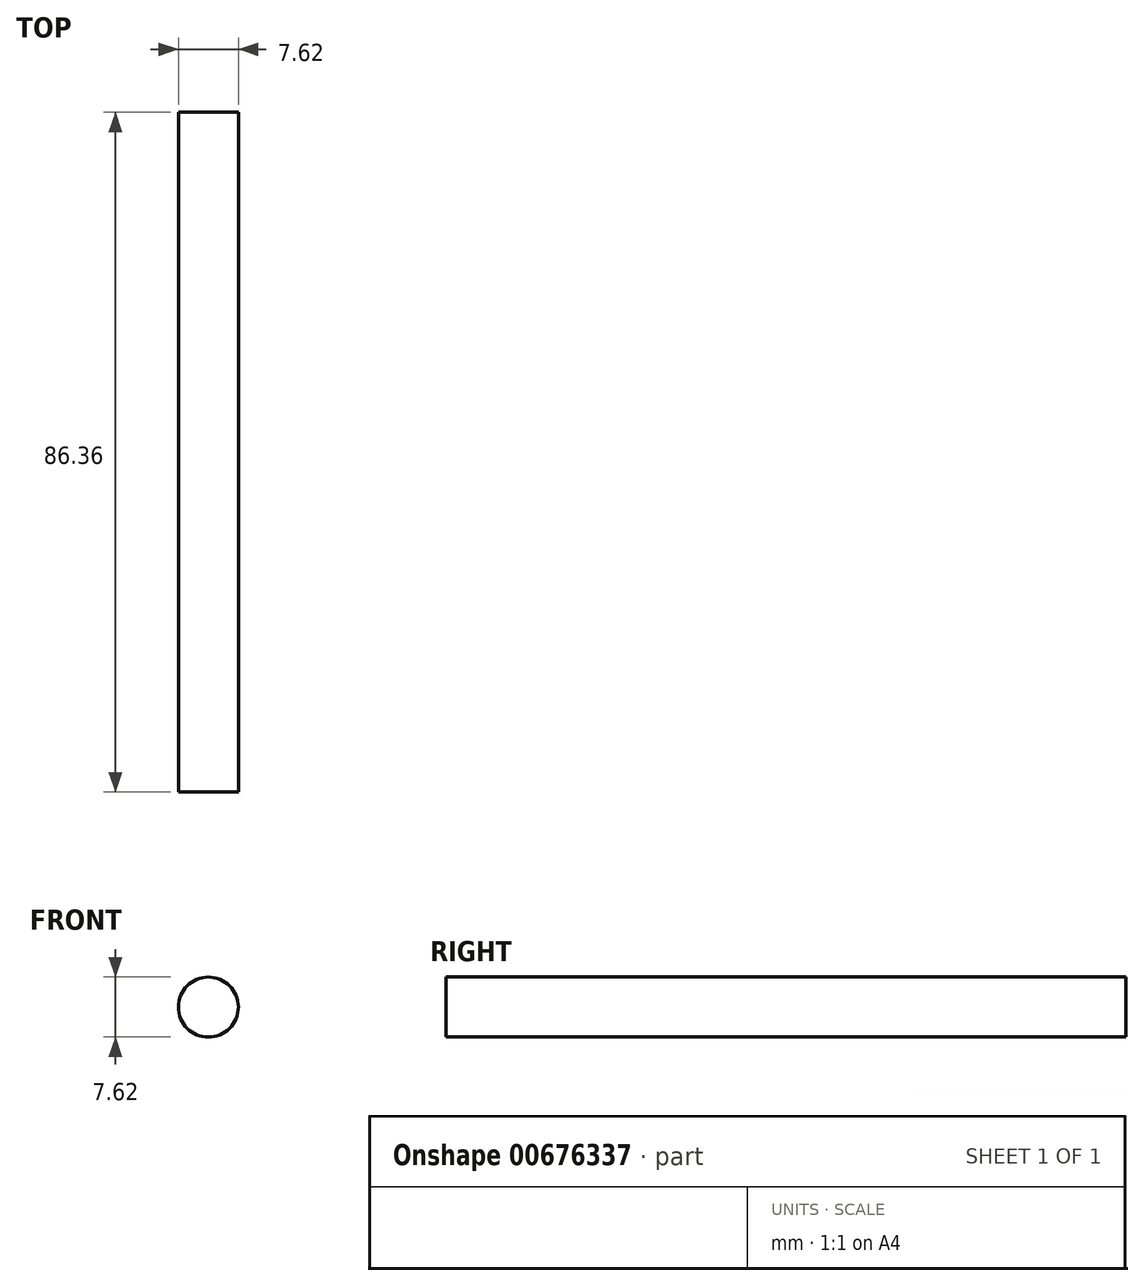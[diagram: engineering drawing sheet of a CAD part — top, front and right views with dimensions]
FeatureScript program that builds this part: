
annotation { "Feature Type Name" : "Feature", "Feature Type Description" : "" }
export const myFeature = defineFeature(function(context is Context, id is Id, definition is map)
    precondition{}
    {
        {
            var Q0;
            Q0=qCreatedBy(makeId("Front.planeOp"),FACE);
            var sketch = newSketch(context, id + "F0", { "sketchPlane" : qUnion([Q0])});
            skCircle(sketch, "E0", {"center": v(0, 0) * mm, "radius": 3.81 * mm});
            skSolve(sketch);
        }
        {
            var Q0;
            Q0 = qSketchRegion(id + "F0", true);
            extrude(context, id + "F1", {"entities" : qUnion([Q0]), "depth" : 86.36 * mm, "offsetDistance" : 25.4 * mm});
        }
    });
